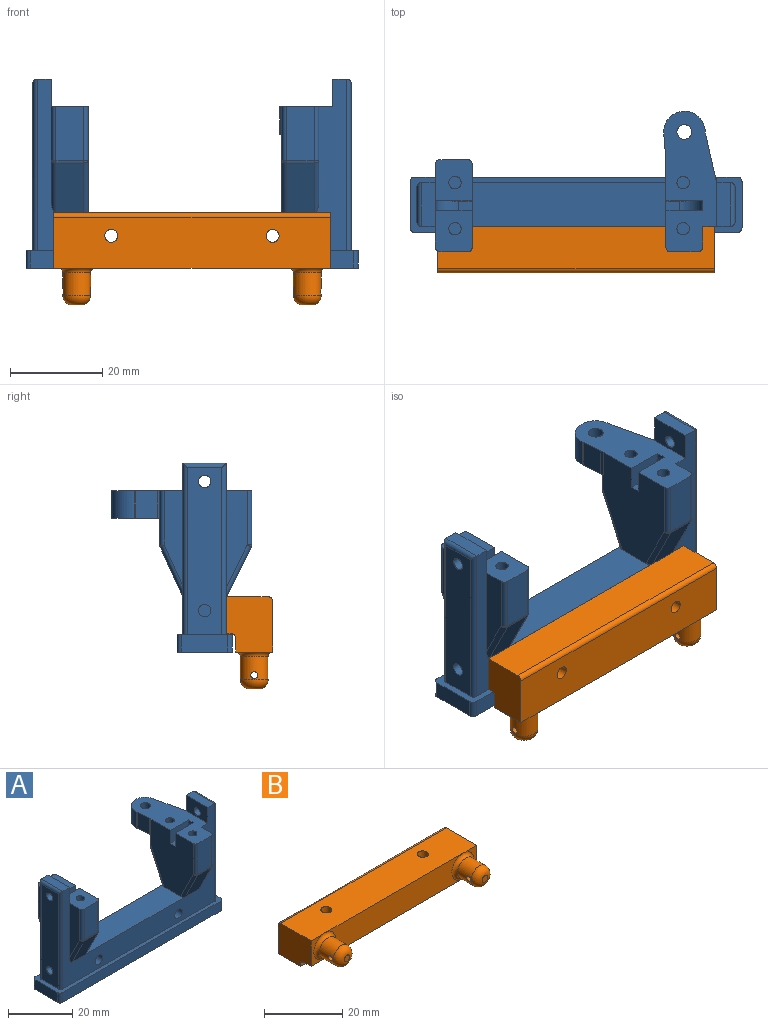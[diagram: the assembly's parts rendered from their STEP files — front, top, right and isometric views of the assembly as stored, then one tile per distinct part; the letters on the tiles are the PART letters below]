
ASSEMBLY  parts=2 mates=1
PART A: 107 faces, bbox 72x30.5x41 mm
  f0: plane 70x3.75mm, normal (0,1,0), area 125.2mm2, adj f95,f96,f97,f98,f104,f105,f106
  f1: plane 67x39.5mm, normal (0,1,0), area 849.7mm2, adj f3,f10,f11,f13,f15,f16,f19,f25
  f2: plane 7x5.78mm, normal (0,1,0), area 40.1mm2, adj f5,f59,f84,f85,f87
  f3: plane 14.58x4mm, normal (1,0,0), area 40.7mm2, adj f1,f59,f83,f84
  f4: plane 9.03x8mm, normal (0,0,1), area 66mm2, adj f6,f11,f22,f23,f33,f47,f69,f72
  f5: plane 23x19mm, normal (-1,0,0), area 352.2mm2, adj f2,f10,f17,f36,f37,f38,f59,f60
  f6: plane 23x18mm, normal (1,0,0), area 343.8mm2, adj f4,f10,f27,f33,f34,f35,f69,f70
  f7: cylinder r=1.7mm len=8.5mm, axis (0,-1,0), area 90.8mm2, adj f9,f32
  f8: cylinder r=1.7mm len=8.5mm, axis (0,-1,0), area 90.8mm2, adj f9,f30
  f9: plane 67x37.25mm, normal (0,-1,0), area 778.6mm2, adj f7,f8,f10,f11,f13,f15,f16,f17
  f10: plane 44x9.5mm, normal (0,0,1), area 400mm2, adj f1,f5,f6,f9,f70,f76,f85,f88
  f11: plane 9.5x6mm, normal (1,0,0), area 51.3mm2, adj f1,f4,f9,f13,f27,f40,f54
  f12: plane 36.25x7.5mm, normal (-1,0,0), area 260.4mm2, adj f52,f54,f66,f67,f68,f95
  f13: plane 9.5x3mm, normal (0,0,1), area 28.5mm2, adj f1,f9,f11,f67
  f14: plane 36.25x7.5mm, normal (1,0,0), area 260.4mm2, adj f49,f50,f63,f64,f65,f95
  f15: plane 9.5x6mm, normal (-1,0,0), area 51.3mm2, adj f1,f9,f16,f17,f49
  f16: plane 9.5x3mm, normal (0,0,1), area 28.5mm2, adj f1,f9,f15,f64
  f17: plane 30.5x11.5mm, normal (0,0,1), area 253.2mm2, adj f5,f9,f15,f18,f21,f36,f37,f39
  f18: plane 20.76x4.5mm, normal (1,0,0), area 73.2mm2, adj f9,f17,f90,f91
  f19: plane 10.8x6mm, normal (0,0.91,-0.41), area 71.2mm2, adj f1,f83,f85,f87
  f20: plane 10.79x6mm, normal (0,-0.89,-0.45), area 72.4mm2, adj f9,f88,f91,f94
  f21: plane 11.76x6mm, normal (0,-1,0), area 70.6mm2, adj f17,f89,f90,f94
  f22: plane 20.76x4.5mm, normal (-1,0,0), area 73.2mm2, adj f4,f9,f71,f72
  f23: plane 11.76x6mm, normal (0,-1,0), area 70.6mm2, adj f4,f69,f72,f75
  f24: plane 10.79x6mm, normal (0,-0.89,-0.45), area 72.4mm2, adj f9,f70,f71,f75
  f25: plane 10.8x6mm, normal (0,0.91,-0.41), area 71.2mm2, adj f1,f76,f79,f82
  f26: plane 11.78x6mm, normal (0,1,0), area 70.7mm2, adj f27,f77,f78,f82
  f27: plane 8.97x8mm, normal (0,0,1), area 65.6mm2, adj f6,f11,f26,f28,f34,f41,f77,f78
  f28: plane 20.58x4mm, normal (-1,0,0), area 64.7mm2, adj f1,f27,f78,f79
  f29: cylinder r=3.25mm len=6.5mm, axis (0,1,0), area 20.4mm2, adj f1,f30
  f30: plane 6.5x6.5mm, normal (0,1,0), area 24.1mm2, adj f8,f29
  f31: cylinder r=3.25mm len=6.5mm, axis (0,1,0), area 20.4mm2, adj f1,f32
  f32: plane 6.5x6.5mm, normal (0,1,0), area 24.1mm2, adj f7,f31
  f33: plane 8x5mm, normal (0,1,0), area 34.6mm2, adj f4,f6,f35,f40
  f34: plane 8x5mm, normal (0,-1,0), area 34.6mm2, adj f6,f27,f35,f40
  f35: plane 3x2mm, normal (0,0,1), area 6mm2, adj f6,f33,f34,f40
  f36: plane 8x5mm, normal (0,1,0), area 34.6mm2, adj f5,f17,f38,f39
  f37: plane 8x5mm, normal (0,-1,0), area 34.6mm2, adj f5,f17,f38,f39
  f38: plane 3x2mm, normal (0,0,1), area 6mm2, adj f5,f36,f37,f39
  f39: cylinder r=5mm len=5mm, axis (0,1,0), area 15.7mm2, adj f17,f36,f37,f38
  f40: cylinder r=5mm len=5mm, axis (0,-1,0), area 15.7mm2, adj f11,f33,f34,f35
  f41: cylinder r=1.35mm len=10mm, axis (0,0,1), area 84.8mm2, adj f27,f42
  f42: plane 2.7x2.7mm, normal (0,0,1), area 5.7mm2, adj f41
  f43: cylinder r=1.35mm len=10mm, axis (0,0,1), area 84.8mm2, adj f17,f44
  f44: plane 2.7x2.7mm, normal (0,0,1), area 5.7mm2, adj f43
  f45: cylinder r=1.35mm len=10mm, axis (0,0,1), area 84.8mm2, adj f17,f46
  f46: plane 2.7x2.7mm, normal (0,0,1), area 5.7mm2, adj f45
  f47: cylinder r=1.35mm len=10mm, axis (0,0,1), area 84.8mm2, adj f4,f48
  f48: plane 2.7x2.7mm, normal (0,0,1), area 5.7mm2, adj f47
  f49: cylinder r=1.35mm len=4mm, axis (1,0,0), area 33.9mm2, adj f14,f15
  f50: cylinder r=1.35mm len=10mm, axis (1,0,0), area 84.8mm2, adj f14,f51
  f51: plane 2.7x2.7mm, normal (1,0,0), area 5.7mm2, adj f50
  f52: cylinder r=1.35mm len=10mm, axis (-1,0,0), area 84.8mm2, adj f12,f53
  f53: plane 2.7x2.7mm, normal (-1,0,0), area 5.7mm2, adj f52
  f54: cylinder r=1.35mm len=4mm, axis (-1,0,0), area 33.9mm2, adj f11,f12
  f55: plane 6x4.92mm, normal (-1,-0.09,0), area 29.6mm2, adj f17,f59,f60,f62
  f56: plane 10.28x6mm, normal (0.98,0.22,0), area 63.3mm2, adj f1,f17,f59,f61
  f57: cylinder r=4.5mm len=8.98mm, axis (0,0,1), area 85.2mm2, adj f17,f59,f61,f62
  f58: cylinder r=1.6mm len=6mm, axis (0,0,1), area 60.3mm2, adj f17,f59
  f59: plane 15.5x11.5mm, normal (0,0,-1), area 92.8mm2, adj f1,f2,f3,f5,f55,f56,f57,f58
  f60: cylinder r=9mm len=6mm, axis (0,0,1), area 4.6mm2, adj f5,f17,f55,f59
  f61: cylinder r=9mm len=6mm, axis (0,0,1), area 7mm2, adj f17,f56,f57,f59
  f62: cylinder r=9mm len=6mm, axis (0,0,1), area 1.3mm2, adj f17,f55,f57,f59
  f63: cylinder r=1mm len=37.25mm, axis (0,0,1), area 57.9mm2, adj f9,f14,f64,f95
  f64: cylinder r=1mm len=9.5mm, axis (0,-1,0), area 13.8mm2, adj f14,f16,f63,f65
  f65: cylinder r=1mm len=37.25mm, axis (0,0,-1), area 57.9mm2, adj f1,f14,f64,f95
  f66: cylinder r=1mm len=37.25mm, axis (0,0,1), area 57.9mm2, adj f1,f12,f67,f95
  f67: cylinder r=1mm len=9.5mm, axis (0,1,0), area 13.8mm2, adj f12,f13,f66,f68
  f68: cylinder r=1mm len=37.25mm, axis (0,0,-1), area 57.9mm2, adj f9,f12,f67,f95
  f69: cylinder r=1mm len=11.76mm, axis (0,0,1), area 18.5mm2, adj f4,f6,f23,f73
  f70: cylinder r=1mm len=11.68mm, axis (0,-0.45,0.89), area 19.2mm2, adj f6,f10,f24,f73
  f71: cylinder r=1mm len=11.24mm, axis (0,0.45,-0.89), area 17.8mm2, adj f9,f22,f24,f74
  f72: cylinder r=1mm len=11.76mm, axis (0,0,-1), area 18.5mm2, adj f4,f22,f23,f74
  f73: sphere r=1mm, area 0.5mm2, adj f69,f70,f75
  f74: sphere r=1mm, area 0.5mm2, adj f71,f72,f75
  f75: cylinder r=1mm len=6mm, axis (1,0,0), area 2.8mm2, adj f23,f24,f73,f74
  f76: cylinder r=1mm len=11.63mm, axis (0,-0.41,-0.91), area 18.9mm2, adj f6,f10,f25,f80
  f77: cylinder r=1mm len=11.78mm, axis (0,0,-1), area 18.5mm2, adj f6,f26,f27,f80
  f78: cylinder r=1mm len=11.78mm, axis (0,0,1), area 18.5mm2, adj f26,f27,f28,f81
  f79: cylinder r=1mm len=11.22mm, axis (0,0.41,0.91), area 17.4mm2, adj f1,f25,f28,f81
  f80: sphere r=1mm, area 0.4mm2, adj f76,f77,f82
  f81: sphere r=1mm, area 0.4mm2, adj f78,f79,f82
  f82: cylinder r=1mm len=6mm, axis (1,0,0), area 2.6mm2, adj f25,f26,f80,f81
  f83: cylinder r=1mm len=11.22mm, axis (0,-0.41,-0.91), area 17.4mm2, adj f1,f3,f19,f86
  f84: cylinder r=1mm len=5.78mm, axis (0,0,-1), area 9.1mm2, adj f2,f3,f59,f86
  f85: cylinder r=1mm len=13.83mm, axis (0,0.41,0.91), area 20.5mm2, adj f2,f5,f10,f19,f87
  f86: sphere r=1mm, area 0.4mm2, adj f83,f84,f87
  f87: cylinder r=1mm len=6.41mm, axis (-1,0,0), area 2.6mm2, adj f2,f19,f85,f86
  f88: cylinder r=1mm len=11.68mm, axis (0,0.45,-0.89), area 19.2mm2, adj f5,f10,f20,f92
  f89: cylinder r=1mm len=11.76mm, axis (0,0,-1), area 18.5mm2, adj f5,f17,f21,f92
  f90: cylinder r=1mm len=11.76mm, axis (0,0,1), area 18.5mm2, adj f17,f18,f21,f93
  f91: cylinder r=1mm len=11.24mm, axis (0,-0.45,0.89), area 17.8mm2, adj f9,f18,f20,f93
  f92: sphere r=1mm, area 0.5mm2, adj f88,f89,f94
  f93: sphere r=1mm, area 0.5mm2, adj f90,f91,f94
  f94: cylinder r=1mm len=6mm, axis (-1,0,0), area 2.8mm2, adj f20,f21,f92,f93
  f95: plane 72x12mm, normal (0,0,1), area 132.2mm2, adj f0,f1,f9,f12,f14,f63,f65,f66
  f96: plane 72x12mm, normal (0,0,-1), area 863.1mm2, adj f0,f97,f98,f99,f100,f101,f102,f103
  f97: cylinder r=1mm len=3.75mm, axis (0,0,-1), area 5.9mm2, adj f0,f95,f96,f103
  f98: cylinder r=1mm len=3.75mm, axis (0,0,1), area 5.9mm2, adj f0,f95,f96,f99
  f99: plane 10x3.75mm, normal (1,0,0), area 37.5mm2, adj f95,f96,f98,f100
  f100: cylinder r=1mm len=3.75mm, axis (0,0,-1), area 5.9mm2, adj f95,f96,f99,f101
  f101: plane 70x3.75mm, normal (0,-1,0), area 262.5mm2, adj f95,f96,f100,f102
  f102: cylinder r=1mm len=3.75mm, axis (0,0,1), area 5.9mm2, adj f95,f96,f101,f103
  f103: plane 10x3.75mm, normal (-1,0,0), area 37.5mm2, adj f95,f96,f97,f102
  f104: plane 2.25x1.25mm, normal (-1,0,0), area 2.8mm2, adj f0,f1,f95,f105
  f105: plane 61x1.25mm, normal (0,0,1), area 76.3mm2, adj f0,f1,f104,f106
  f106: plane 2.25x1.25mm, normal (1,0,0), area 2.8mm2, adj f0,f1,f95,f105
PART B: 24 faces, bbox 60.2x20x11.1 mm
  f0: plane 8x5mm, normal (0,-1,0), area 14.9mm2, adj f4,f8,f10,f18
  f1: plane 50x8mm, normal (0,-1,0), area 349.7mm2, adj f8,f10,f18,f19
  f2: plane 60x1mm, normal (0,-1,0), area 60mm2, adj f4,f7,f9,f20
  f3: plane 60x9mm, normal (0,1,0), area 540mm2, adj f4,f7,f9,f21
  f4: plane 12x10mm, normal (-1,0,0), area 112mm2, adj f0,f2,f3,f8,f9,f10,f20,f21
  f5: cylinder r=1.4mm len=10mm, axis (0,0,-1), area 88mm2, adj f8,f9
  f6: cylinder r=1.4mm len=10mm, axis (0,0,-1), area 88mm2, adj f8,f9
  f7: plane 12x10mm, normal (1,0,0), area 112mm2, adj f2,f3,f8,f9,f10,f11,f20,f21
  f8: plane 60x11mm, normal (0,0,1), area 647.7mm2, adj f0,f1,f4,f5,f6,f7,f11,f21
  f9: plane 60x8mm, normal (0,0,-1), area 467.7mm2, adj f2,f3,f4,f5,f6,f7
  f10: plane 60x3mm, normal (0,0,-1), area 180mm2, adj f0,f1,f4,f7,f11,f20
  f11: plane 8x5mm, normal (0,-1,0), area 14.9mm2, adj f7,f8,f10,f19
  f12: cylinder r=3mm len=6mm, axis (0,1,0), area 90.7mm2, adj f17,f18,f23
  f13: plane 2x2mm, normal (0,-1,0), area 3.1mm2, adj f17
  f14: cylinder r=3mm len=6mm, axis (0,1,0), area 90.7mm2, adj f16,f19,f22
  f15: plane 2x2mm, normal (0,-1,0), area 3.1mm2, adj f16
  f16: torus R=1mm, axis (0,-1,0), area 44.9mm2, adj f14,f15
  f17: torus R=1mm, axis (0,-1,0), area 44.9mm2, adj f12,f13
  f18: torus R=4mm, axis (0,-1,0), area 33.2mm2, adj f0,f1,f12
  f19: torus R=4mm, axis (0,-1,0), area 33.2mm2, adj f1,f11,f14
  f20: cylinder r=1mm len=60mm, axis (-1,0,0), area 94.2mm2, adj f2,f4,f7,f10
  f21: cylinder r=1mm len=60mm, axis (1,0,0), area 94.2mm2, adj f3,f4,f7,f8
  f22: cylinder r=0.75mm len=6mm, axis (-1,0,0), area 27.8mm2, adj f14
  f23: cylinder r=0.75mm len=6mm, axis (-1,0,0), area 27.8mm2, adj f12
PLACE A at identity
PLACE B rot(axis=(1,0,0),90deg) t=(36,1.25,-8.77)mm
MATE cylindrical B.f6 <-> A.f8  axis (0,1,0) through (18.5,1.25,7)mm
